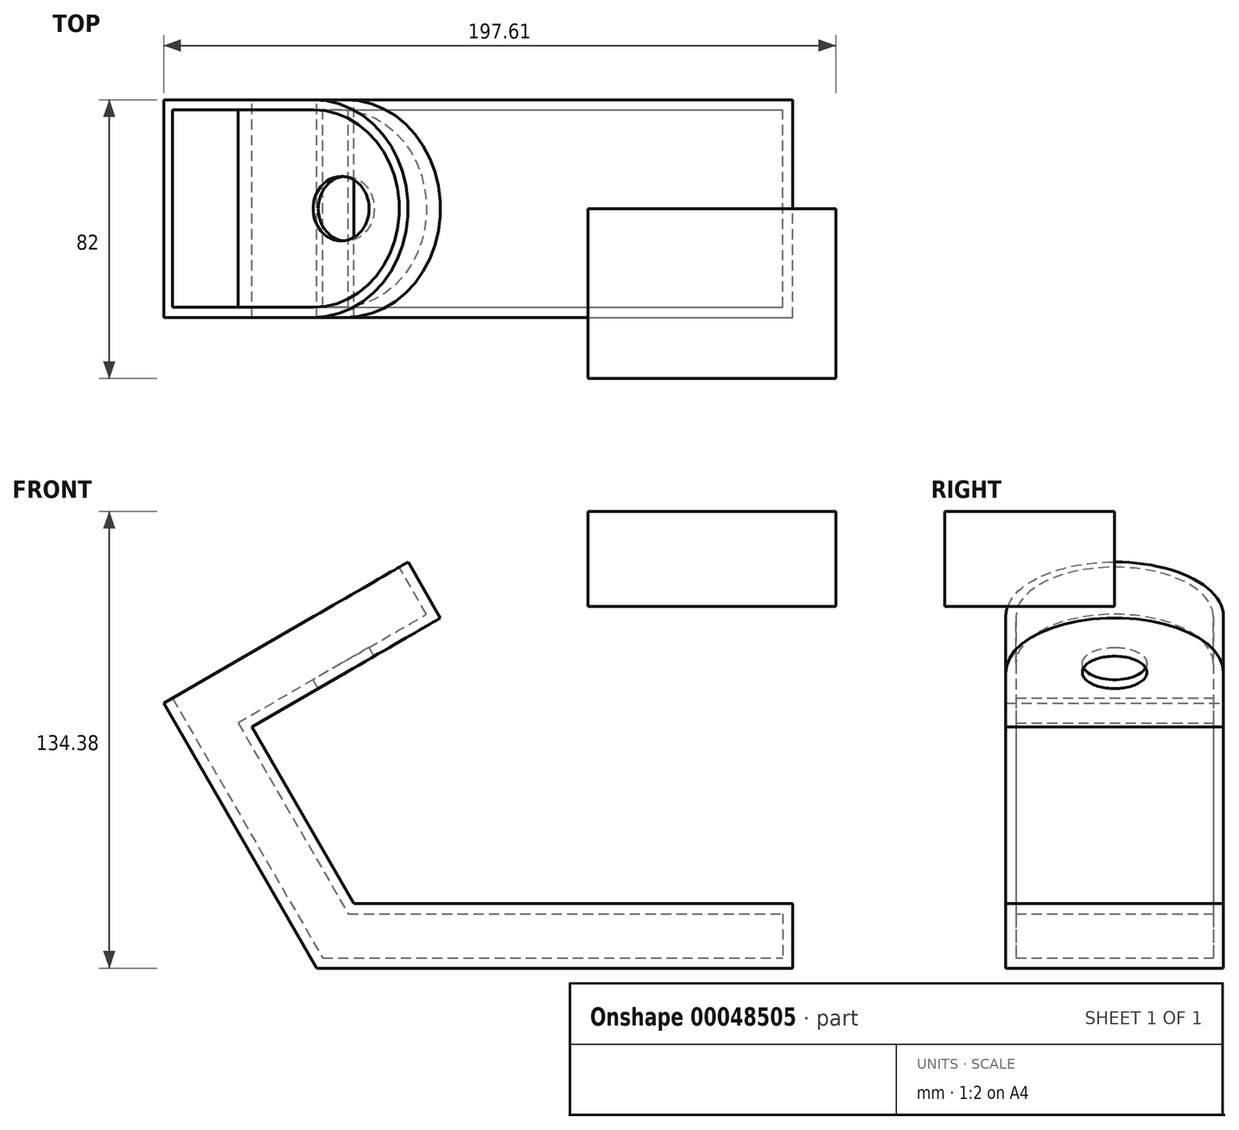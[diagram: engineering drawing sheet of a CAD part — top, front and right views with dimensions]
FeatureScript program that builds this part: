
annotation { "Feature Type Name" : "Feature", "Feature Type Description" : "" }
export const myFeature = defineFeature(function(context is Context, id is Id, definition is map)
    precondition{}
    {
        {
            var Q0;
            Q0=qCreatedBy(makeId("Front.planeOp"),FACE);
            var sketch = newSketch(context, id + "F0", { "sketchPlane" : qUnion([Q0])});
            skLineSegment(sketch, "E0", {"start": v(0, 0) * mm, "end": v(140, 0) * mm});
            skLineSegment(sketch, "E1", {"start": v(26.88, 119.44) * mm, "end": v(-45, 77.94) * mm});
            skLineSegment(sketch, "E2", {"start": v(-45, 77.94) * mm, "end": v(0, 0) * mm});
            skLineSegment(sketch, "E3.0", {"start": v(10.97, 19) * mm, "end": v(140, 19) * mm});
            skLineSegment(sketch, "E3.1", {"start": v(-19.05, 70.99) * mm, "end": v(10.97, 19) * mm});
            skLineSegment(sketch, "E3.2", {"start": v(36.38, 102.99) * mm, "end": v(-19.05, 70.99) * mm});
            skLineSegment(sketch, "E4", {"start": v(26.88, 119.44) * mm, "end": v(36.38, 102.99) * mm});
            skLineSegment(sketch, "E5", {"start": v(140, 19) * mm, "end": v(140, 0) * mm});
            skSolve(sketch);
        }
        {
            var Q0;
            Q0=makeQuery(id+"F0.imprint","IMPRINT",FACE,{"disambiguationData":[TD([[makeQuery(id+"F0.imprint","IMPRINT",EDGE,{"derivedFrom":sQuery(id+"F0.wireOp",EDGE,"E0")}),1.0]])]});
            extrude(context, id + "F1", {"entities" : qUnion([Q0]), "endBound" : BoundingType.SYMMETRIC, "depth" : 64 * mm});
        }
        {
            var Q0;
            Q0=makeQuery(id+"F1.opExtrude","SWEPT_FACE",FACE,{"disambiguationData":[OSD([sQuery(id+"F0.wireOp",EDGE,"E1")])]});
            var sketch = newSketch(context, id + "F2", { "sketchPlane" : qUnion([Q0])});
            skPoint(sketch, "E6", {"position": v(51, 0) * mm});
            skCircle(sketch, "E7", {"center": v(51, 0) * mm, "radius": 32 * mm});
            skSolve(sketch);
        }
        {
            var Q0;
            {var subQ0=sQuery(id+"F0.wireOp",EDGE,"E1");var subQ2=sQuery(id+"F2.wireOp",EDGE,"E7");var subQ4=makeQuery(id+"F1.opExtrude","CAP_EDGE",EDGE,{"disambiguationData":[OSD([subQ0])],"isStart":false});var subQ6=makeQuery(id+"F2.imprint","INTERSECT",VERTEX,{"derivedFrom":[subQ4,subQ2]});Q0=makeQuery(id+"F2.imprint","IMPRINT",FACE,{"disambiguationData":[TD([[makeQuery(id+"F2.imprint","IMPRINT",EDGE,{"disambiguationData":[TD([[subQ6,-1.0]])],"derivedFrom":subQ2}),-1.0]])]});}
            var Q1;
            {var subQ0=sQuery(id+"F0.wireOp",EDGE,"E1");var subQ1=makeQuery(id+"F1.opExtrude","CAP_EDGE",EDGE,{"disambiguationData":[OSD([subQ0])],"isStart":true});var subQ2=sQuery(id+"F2.wireOp",EDGE,"E7");var subQ3=makeQuery(id+"F2.imprint","INTERSECT",VERTEX,{"derivedFrom":[subQ1,subQ2]});Q1=makeQuery(id+"F2.imprint","IMPRINT",FACE,{"disambiguationData":[TD([[makeQuery(id+"F2.imprint","IMPRINT",EDGE,{"disambiguationData":[TD([[subQ3,1.0]])],"derivedFrom":subQ2}),-1.0]])]});}
            var Q2;
            Q2=makeQuery(id+"F2.imprint","IMPRINT",FACE,{"disambiguationData":[TD([[makeQuery(id+"F2.imprint","IMPRINT",EDGE,{"derivedFrom":sQuery(id+"F2.wireOp",EDGE,"fa961752-356b-4ab1-98e8-62448cef2765")}),1.0]])]});
            extrude(context, id + "F3", {"entities" : qUnion([Q0, Q1, Q2]), "operationType" : NewBodyOperationType.REMOVE, "endBound" : BoundingType.UP_TO_NEXT, "oppositeDirection" : true, "depth" : 25 * mm});
        }
        {
            var Q0;
            Q0=makeQuery(id+"F1.opExtrude","SWEPT_FACE",FACE,{"disambiguationData":[OSD([sQuery(id+"F0.wireOp",EDGE,"E1")])]});
            shell(context, id + "F4", {"entities" : qUnion([Q0]), "thickness" : 3 * mm});
        }
        {
            var Q0;
            Q0=makeQuery(id+"F4.opShell","OFFSET_FACE",FACE,{"disambiguationData":[OSD([sQuery(id+"F0.wireOp",EDGE,"E3.2")])]});
            var sketch = newSketch(context, id + "F5", { "sketchPlane" : qUnion([Q0])});
            skPoint(sketch, "E8", {"position": v(51, 0) * mm});
            skCircle(sketch, "E9", {"center": v(51, 0) * mm, "radius": 9.5 * mm});
            skSolve(sketch);
        }
        {
            var Q0;
            Q0=makeQuery(id+"F5.imprint","IMPRINT",FACE,{"disambiguationData":[TD([[makeQuery(id+"F5.imprint","IMPRINT",EDGE,{"derivedFrom":sQuery(id+"F5.wireOp",EDGE,"E9")}),1.0]])]});
            extrude(context, id + "F6", {"entities" : qUnion([Q0]), "operationType" : NewBodyOperationType.REMOVE, "endBound" : BoundingType.UP_TO_NEXT, "oppositeDirection" : true, "depth" : 25 * mm});
        }
        {
            var Q0;
            Q0=qCreatedBy(makeId("Front.planeOp"),FACE);
            var sketch = newSketch(context, id + "F7", { "sketchPlane" : qUnion([Q0])});
            skLineSegment(sketch, "E10.bottom", {"start": v(79.74, 106.34) * mm, "end": v(152.6, 106.34) * mm});
            skLineSegment(sketch, "E10.top", {"start": v(79.74, 134.38) * mm, "end": v(152.6, 134.38) * mm});
            skLineSegment(sketch, "E10.left", {"start": v(79.74, 106.34) * mm, "end": v(79.74, 134.38) * mm});
            skLineSegment(sketch, "E10.right", {"start": v(152.6, 106.34) * mm, "end": v(152.6, 134.38) * mm});
            skSolve(sketch);
        }
        {
            var Q0;
            Q0=makeQuery(id+"F7.imprint","IMPRINT",FACE,{"disambiguationData":[TD([[makeQuery(id+"F7.imprint","IMPRINT",EDGE,{"derivedFrom":sQuery(id+"F7.wireOp",EDGE,"E10.bottom")}),1.0]])]});
            extrude(context, id + "F8", {"entities" : qUnion([Q0]), "depth" : 50 * mm});
        }
    });
